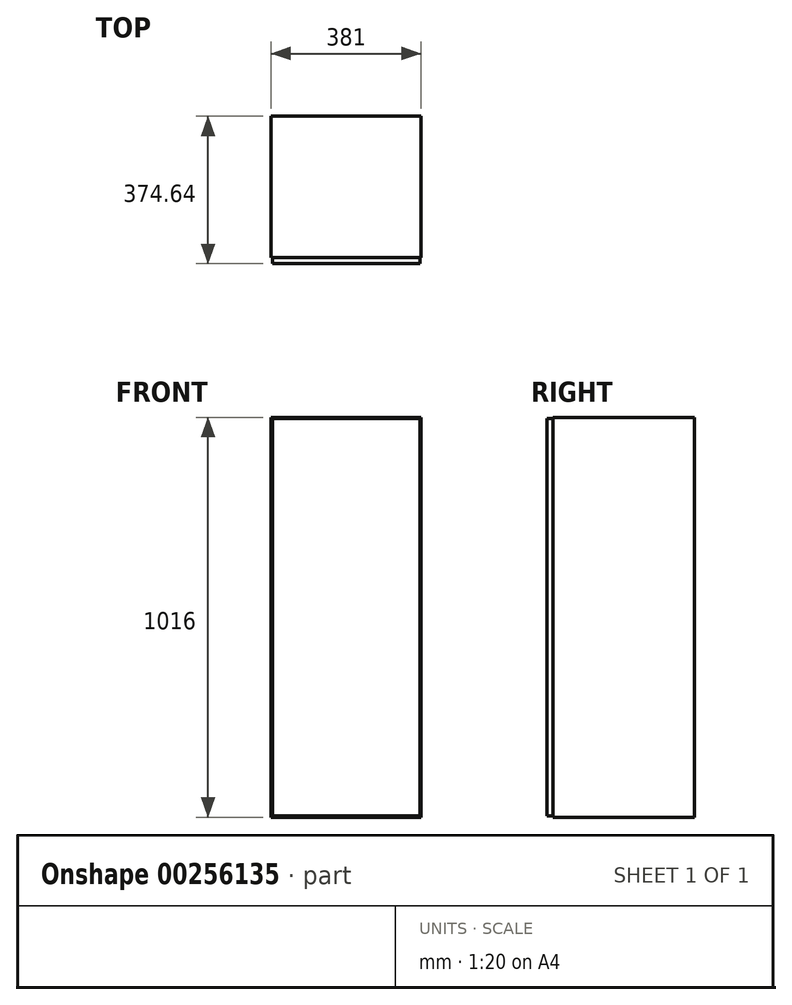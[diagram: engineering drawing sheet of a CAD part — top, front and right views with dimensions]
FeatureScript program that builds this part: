
annotation { "Feature Type Name" : "Feature", "Feature Type Description" : "" }
export const myFeature = defineFeature(function(context is Context, id is Id, definition is map)
    precondition{}
    {
        {
            var Q0;
            Q0=qCreatedBy(makeId("Front.planeOp"),FACE);
            var sketch = newSketch(context, id + "F0", { "sketchPlane" : qUnion([Q0])});
            skLineSegment(sketch, "E0.bottom", {"start": v(190.5, 114.3) * mm, "end": v(-190.5, 114.3) * mm});
            skLineSegment(sketch, "E0.top", {"start": v(190.5, 1130.3) * mm, "end": v(-190.5, 1130.3) * mm});
            skLineSegment(sketch, "E0.left", {"start": v(190.5, 114.3) * mm, "end": v(190.5, 1130.3) * mm});
            skLineSegment(sketch, "E0.right", {"start": v(-190.5, 114.3) * mm, "end": v(-190.5, 1130.3) * mm});
            skPoint(sketch, "E0.middle", {"position": v(0, 622.3) * mm});
            skSolve(sketch);
        }
        {
            var Q0;
            Q0=qSketchRegion(id+"F0",true);
            extrude(context, id + "F1", {"entities" : qUnion([Q0]), "endBound" : BoundingType.SYMMETRIC, "oppositeDirection" : true, "depth" : 374.65 * mm});
        }
        {
            var Q0;
            Q0=makeQuery(id+"F1.opExtrude","CAP_FACE",FACE,{"disambiguationData":[OSD([sQuery(id+"F0.wireOp",EDGE,"E0.bottom"),sQuery(id+"F0.wireOp",EDGE,"E0.top"),sQuery(id+"F0.wireOp",EDGE,"E0.left"),sQuery(id+"F0.wireOp",EDGE,"E0.right")])],"isStart":true});
            var sketch = newSketch(context, id + "F2", { "sketchPlane" : qUnion([Q0])});
            skLineSegment(sketch, "E1.0", {"start": v(187.33, 117.48) * mm, "end": v(187.33, 1127.13) * mm});
            skLineSegment(sketch, "E1.1", {"start": v(-187.32, 117.47) * mm, "end": v(187.33, 117.48) * mm});
            skLineSegment(sketch, "E1.2", {"start": v(-187.32, 1127.13) * mm, "end": v(-187.32, 117.47) * mm});
            skLineSegment(sketch, "E1.3", {"start": v(187.33, 1127.13) * mm, "end": v(-187.32, 1127.13) * mm});
            skSolve(sketch);
        }
        {
            var Q0;
            Q0=makeQuery(id+"F2.imprint","IMPRINT",FACE,{"disambiguationData":[TD([[makeQuery(id+"F2.imprint","IMPRINT",EDGE,{"derivedFrom":sQuery(id+"F2.wireOp",EDGE,"E1.0")}),-1.0]])]});
            extrude(context, id + "F3", {"entities" : qUnion([Q0]), "operationType" : NewBodyOperationType.REMOVE, "oppositeDirection" : true, "depth" : 15.88 * mm});
        }
    });
